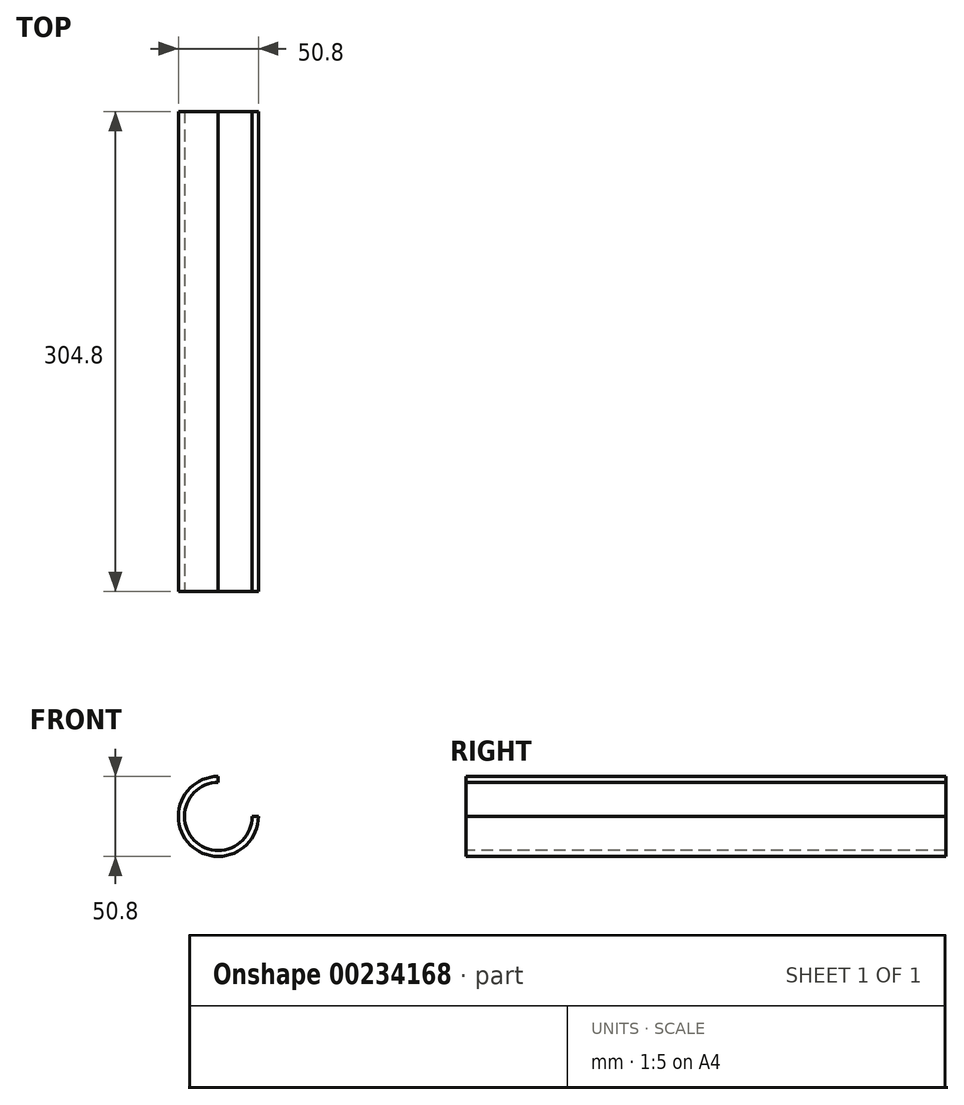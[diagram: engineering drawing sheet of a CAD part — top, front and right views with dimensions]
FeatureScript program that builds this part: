
annotation { "Feature Type Name" : "Feature", "Feature Type Description" : "" }
export const myFeature = defineFeature(function(context is Context, id is Id, definition is map)
    precondition{}
    {
        {
            var Q0;
            Q0=qCreatedBy(makeId("Front.planeOp"),FACE);
            var sketch = newSketch(context, id + "F0", { "sketchPlane" : qUnion([Q0])});
            skCircle(sketch, "E0", {"center": v(0, 0) * mm, "radius": 25.4 * mm});
            skSolve(sketch);
        }
        {
            var Q0;
            Q0=makeQuery(id+"F0.imprint","IMPRINT",FACE,{"disambiguationData":[TD([[makeQuery(id+"F0.imprint","IMPRINT",EDGE,{"derivedFrom":sQuery(id+"F0.wireOp",EDGE,"E0")}),1.0]])]});
            extrude(context, id + "F1", {"entities" : qUnion([Q0]), "endBound" : BoundingType.SYMMETRIC, "depth" : 304.8 * mm});
        }
        {
            var Q0;
            Q0=makeQuery(id+"F1.opExtrude","CAP_FACE",FACE,{"disambiguationData":[OSD([sQuery(id+"F0.wireOp",EDGE,"E0")])],"isStart":false});
            var sketch = newSketch(context, id + "F2", { "sketchPlane" : qUnion([Q0])});
            skLineSegment(sketch, "E1", {"start": v(0, 0) * mm, "end": v(0, 25.4) * mm});
            skLineSegment(sketch, "E2", {"start": v(0, 0) * mm, "end": v(25.4, 0) * mm});
            skCircle(sketch, "E3.0", {"center": v(0, 0) * mm, "radius": 25.4 * mm});
            skSolve(sketch);
        }
        {
            var Q0;
            {var subQ0=sQuery(id+"F2.wireOp",EDGE,"E1");Q0=makeQuery(id+"F2.imprint","IMPRINT",FACE,{"disambiguationData":[TD([[makeQuery(id+"F2.imprint","IMPRINT",EDGE,{"derivedFrom":subQ0}),-1.0]])]});}
            extrude(context, id + "F3", {"entities" : qUnion([Q0]), "operationType" : NewBodyOperationType.REMOVE, "endBound" : BoundingType.THROUGH_ALL, "oppositeDirection" : true, "depth" : 25.4 * mm});
        }
        {
            var Q0;
            Q0=makeQuery(id+"F1.opExtrude","CAP_FACE",FACE,{"disambiguationData":[OSD([sQuery(id+"F0.wireOp",EDGE,"E0")])],"isStart":false});
            var sketch = newSketch(context, id + "F4", { "sketchPlane" : qUnion([Q0])});
            skCircle(sketch, "E4", {"center": v(0, 0) * mm, "radius": 21.59 * mm});
            skSolve(sketch);
        }
        {
            var Q0;
            Q0 = qSketchRegion(id + "F4", true);
            extrude(context, id + "F5", {"entities" : qUnion([Q0]), "operationType" : NewBodyOperationType.REMOVE, "endBound" : BoundingType.THROUGH_ALL, "oppositeDirection" : true, "depth" : 25.4 * mm});
        }
    });
